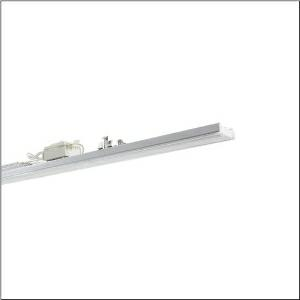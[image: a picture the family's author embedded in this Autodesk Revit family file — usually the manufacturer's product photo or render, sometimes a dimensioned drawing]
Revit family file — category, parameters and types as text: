
# Revit family: licross_r__21_recessed_mo_52tl12dv4fxgd_e48e
name_source: partatom
category: Lighting Fixtures
units: mm (PartAtom-declared; Revit-internal decimal feet)

## family parameters
Cut with Voids When Loaded = No
Host = Face
Light Source = No
Part Type = Normal
Room Calculation Point = No
Round Connector Dimension = Use Diameter
Shared = No

## types (1)
- --- (1 x LED, 15420 lm, 85.3 W, 4000K)
    Apparent Load = 85 VA
    CIE Flux Codes = 72 92 99 100 100
    Color Rendering = 80
    Color Temperature = 4000K
    Default Elevation = 1800 mm
    Description = Licross® 21 Recessed MO, luminaire insert, of sheet steel, galvanised, coil coated, white, length: 2.250mm, width: 66mm, height: 67mm, LED rated luminous flux: 15.420lm, light colour: 840, control gear: DALI 2 (for two DALI lines), with plug, 6-pole, with phase selection, mains connection: 220..240V, AC/DC, 0/50..60Hz, rated input power: 85W, without changeover relay, for emergency light function, for central battery installations according to DIN EN 60598-2-22, halogen-free wiring, primary optical cover: cover, of PMMA, light emission: direct distribution, primary light characteristic: symmetric, protection rating (complete): IP40, insulation class (complete): insulation class I (protective earthing), certification: CE, ENEC, VDE, UKCA, protection symbol: D if used in an environment without relevant dust loads with corresponding accessories, impact resistance: IK06, permissible ambient temperature for indoor applications: -25..+35°C, standard: EN 60598-2-22, corresponds to IFS (International Featured Standards) requirements for safety and quality in the food industry, reducing of maximum allowable ambient temperature of 5°C with ceiling mounting, LABS conformity tested according to VDMA 24364:2018-05, packaging unit: 1 piece
    Height = 58 mm
    Lamp = 1 x LED
    Lamp Light Flux = 15420 lm
    Lamp Power = 85.3 W
    Lamp count = 1
    Length = 2250 mm
    Luminous efficacy = 181 lm/W
    Manufacturer = Siteco
    ModVariant = No
    Model = 52TL12DV4FXGD
    Mounting Place = Ceiling
    Mounting Type = Pendant
    Number of Poles = 1
    OnlyDefault = Yes
    Power Factor = 1
    Product Name = Licross® 21 Recessed MO
    Product group = luminaire insert
    ProductGroupID = 902
    Protection Class = Protection class I
    Protection Degree = IP 40
    RLX_Detail_Level = 1
    RLX_Emergency_Light_Flux = 0 lm
    RLX_Emergency_Type = 0
    RLX_Emergency_Type_DB = No
    RlxData = <blob elided: 30041 chars, md5=3f733165>
    Socket = socket
    Standby Power = 0 W
    System Light Flux = 15420 lm
    System Power = 85 W
    Type Comments = : AC-mode, luminous flux: 100 % | dim-lin: 254 | 390 mA
    Type Image = l_1296930.jpg
    URL = http://relux.com
    VarID = @adj_113102
    Voltage = 0 V
    Weight = 0.00 kg
    Width = 66 mm

## geometry (parser evidence)
native form markers: Blend x4, Sweep x8
no freeform markers — native parametric forms only
